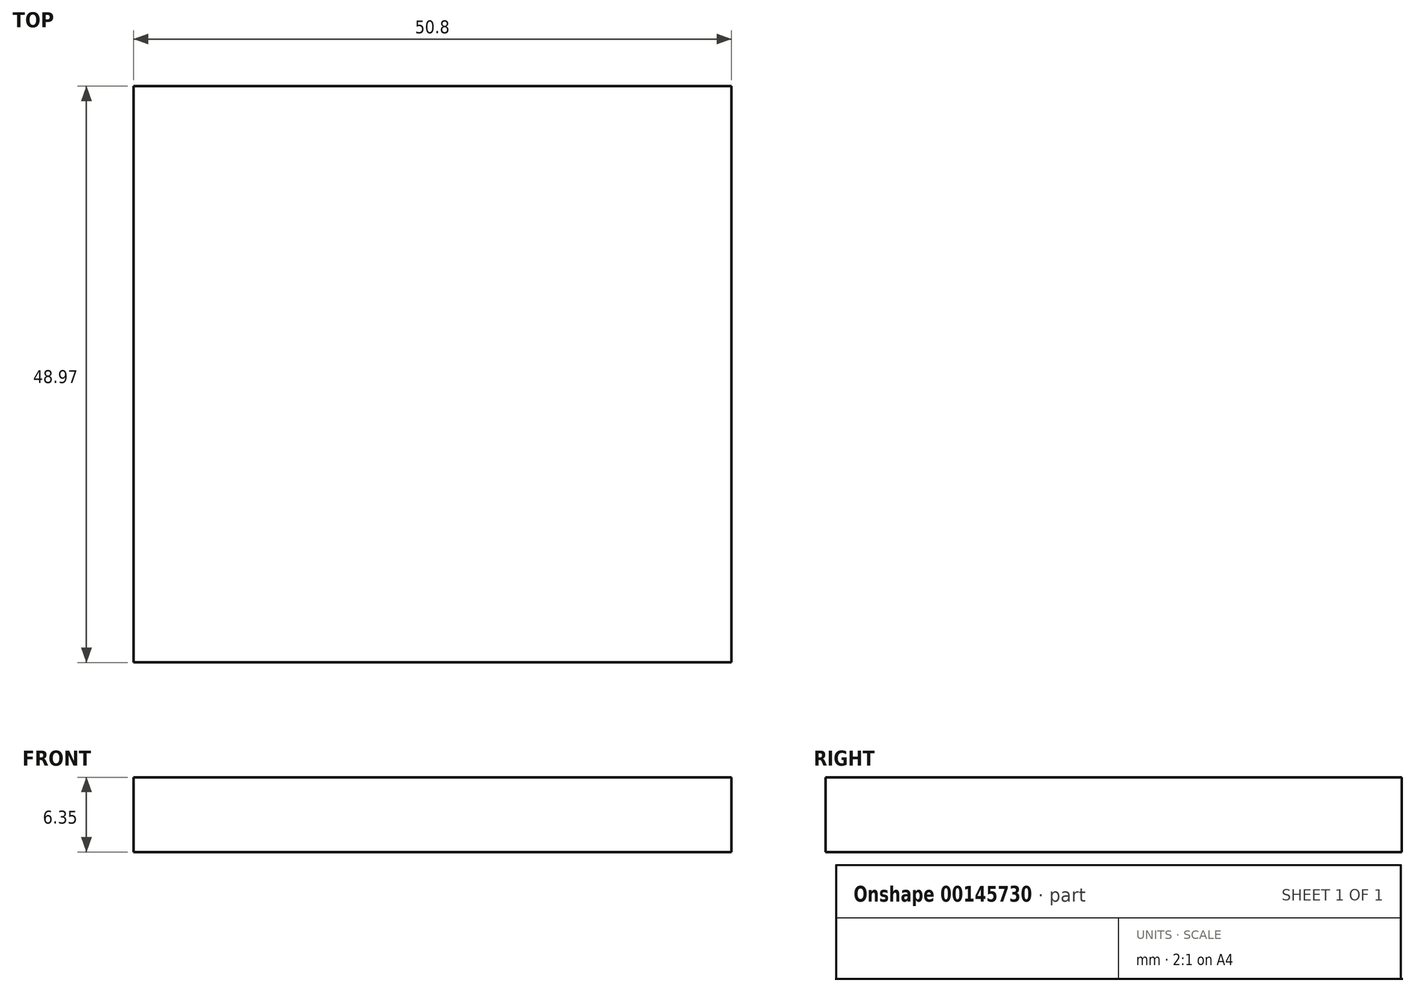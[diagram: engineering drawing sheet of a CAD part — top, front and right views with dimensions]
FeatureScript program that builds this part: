
annotation { "Feature Type Name" : "Feature", "Feature Type Description" : "" }
export const myFeature = defineFeature(function(context is Context, id is Id, definition is map)
    precondition{}
    {
        {
            var Q0;
            Q0=qCreatedBy(makeId("Top.planeOp"),FACE);
            var sketch = newSketch(context, id + "F0", { "sketchPlane" : qUnion([Q0])});
            skLineSegment(sketch, "E0.bottom", {"start": v(-21.54, 8.32) * mm, "end": v(29.26, 8.32) * mm});
            skLineSegment(sketch, "E0.top", {"start": v(-21.54, 57.29) * mm, "end": v(29.26, 57.29) * mm});
            skLineSegment(sketch, "E0.left", {"start": v(-21.54, 8.32) * mm, "end": v(-21.54, 57.29) * mm});
            skLineSegment(sketch, "E0.right", {"start": v(29.26, 8.32) * mm, "end": v(29.26, 57.29) * mm});
            skSolve(sketch);
        }
        {
            var Q0;
            Q0=makeQuery(id+"F0.imprint","IMPRINT",FACE,{"disambiguationData":[TD([[makeQuery(id+"F0.imprint","IMPRINT",EDGE,{"derivedFrom":sQuery(id+"F0.wireOp",EDGE,"E0.bottom")}),1.0]])]});
            extrude(context, id + "F1", {"entities" : qUnion([Q0]), "depth" : 6.35 * mm});
        }
    });
